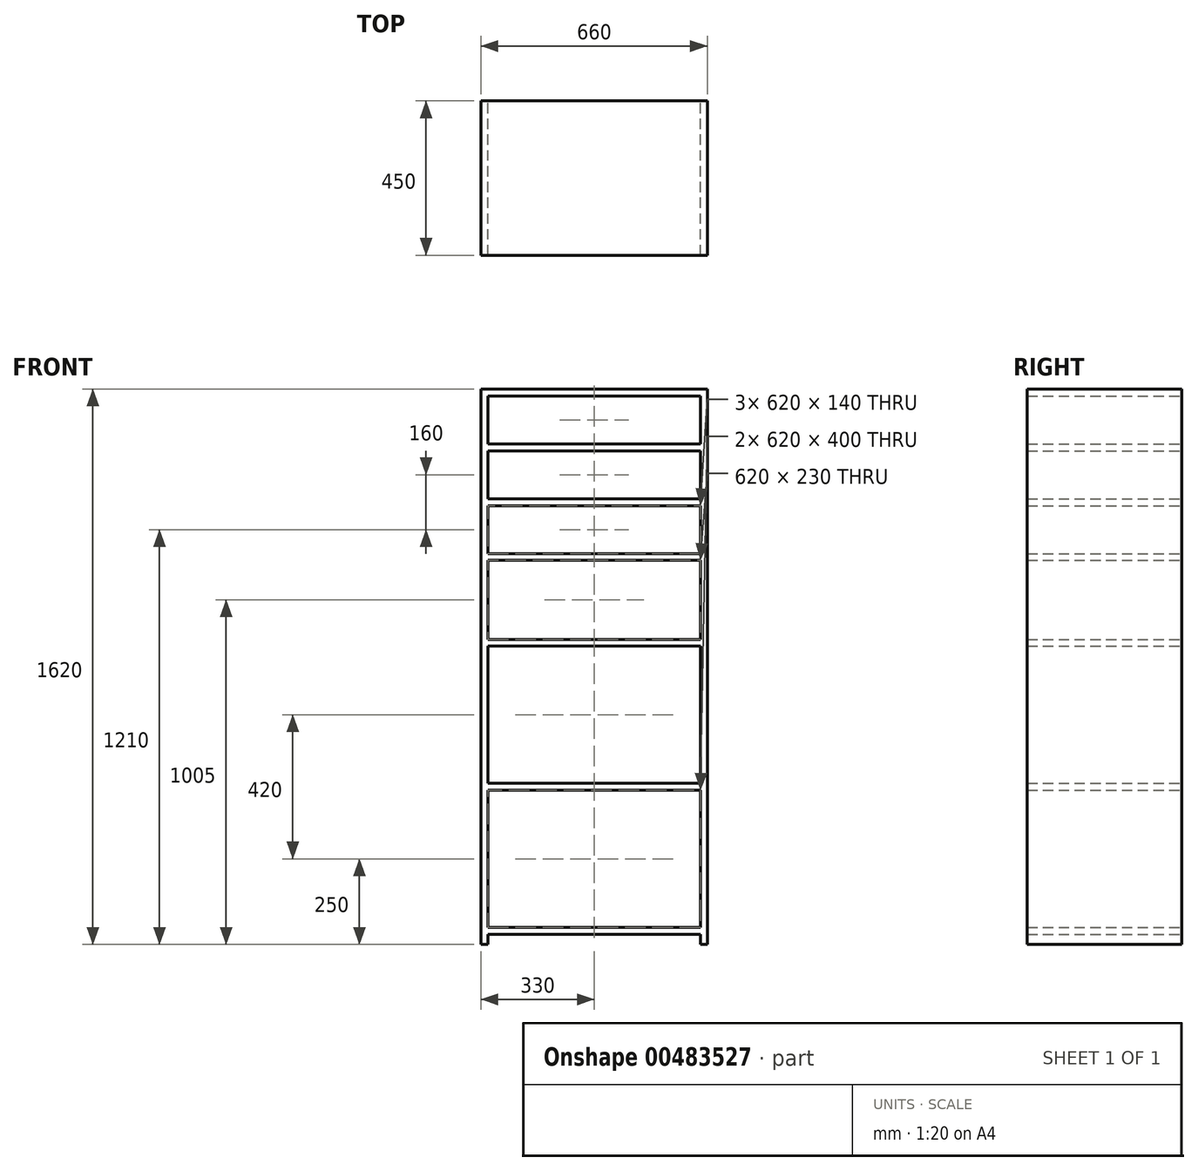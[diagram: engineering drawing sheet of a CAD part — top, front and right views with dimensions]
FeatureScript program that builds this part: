
annotation { "Feature Type Name" : "Feature", "Feature Type Description" : "" }
export const myFeature = defineFeature(function(context is Context, id is Id, definition is map)
    precondition{}
    {
        {
            var Q0;
            Q0=qCreatedBy(makeId("Front.planeOp"),FACE);
            var sketch = newSketch(context, id + "F0", { "sketchPlane" : qUnion([Q0])});
            skLineSegment(sketch, "E0", {"start": v(0, 0) * mm, "end": v(0, 1620) * mm});
            skLineSegment(sketch, "E1", {"start": v(0, 1620) * mm, "end": v(660, 1620) * mm});
            skLineSegment(sketch, "E2", {"start": v(660, 1620) * mm, "end": v(660, 0) * mm});
            skLineSegment(sketch, "E3", {"start": v(660, 0) * mm, "end": v(640, 0) * mm});
            skLineSegment(sketch, "E4", {"start": v(640, 0) * mm, "end": v(640, 30) * mm});
            skLineSegment(sketch, "E5", {"start": v(640, 1600) * mm, "end": v(20, 1600) * mm});
            skLineSegment(sketch, "E6", {"start": v(20, 1600) * mm, "end": v(20, 1460) * mm});
            skLineSegment(sketch, "E7", {"start": v(20, 0) * mm, "end": v(0, 0) * mm});
            skLineSegment(sketch, "E8", {"start": v(640, 1460) * mm, "end": v(20, 1460) * mm});
            skLineSegment(sketch, "E9", {"start": v(640, 1440) * mm, "end": v(20, 1440) * mm});
            skLineSegment(sketch, "E10", {"start": v(640, 1300) * mm, "end": v(20, 1300) * mm});
            skLineSegment(sketch, "E11", {"start": v(640, 1280) * mm, "end": v(20, 1280) * mm});
            skLineSegment(sketch, "E12", {"start": v(640, 1140) * mm, "end": v(20, 1140) * mm});
            skLineSegment(sketch, "E13", {"start": v(640, 1120) * mm, "end": v(20, 1120) * mm});
            skLineSegment(sketch, "E14.trimOffspring", {"start": v(640, 1460) * mm, "end": v(640, 1600) * mm});
            skLineSegment(sketch, "E15.trimOffspring", {"start": v(20, 1440) * mm, "end": v(20, 1300) * mm});
            skLineSegment(sketch, "E16.trimOffspring", {"start": v(20, 1280) * mm, "end": v(20, 1140) * mm});
            skLineSegment(sketch, "E17.trimOffspring", {"start": v(640, 1300) * mm, "end": v(640, 1440) * mm});
            skLineSegment(sketch, "E18.trimOffspring", {"start": v(640, 1140) * mm, "end": v(640, 1280) * mm});
            skLineSegment(sketch, "E19.trimOffspring", {"start": v(20, 1120) * mm, "end": v(20, 890) * mm});
            skLineSegment(sketch, "E20", {"start": v(20, 30) * mm, "end": v(640, 30) * mm});
            skLineSegment(sketch, "E21", {"start": v(20, 50) * mm, "end": v(640, 50) * mm});
            skLineSegment(sketch, "E22", {"start": v(20, 450) * mm, "end": v(640, 450) * mm});
            skLineSegment(sketch, "E23", {"start": v(640, 470) * mm, "end": v(20, 470) * mm});
            skLineSegment(sketch, "E24.trimOffspring", {"start": v(20, 450) * mm, "end": v(20, 50) * mm});
            skLineSegment(sketch, "E25.trimOffspring", {"start": v(20, 30) * mm, "end": v(20, 0) * mm});
            skLineSegment(sketch, "E26.trimOffspring", {"start": v(640, 50) * mm, "end": v(640, 450) * mm});
            skLineSegment(sketch, "E27.trimOffspring", {"start": v(640, 470) * mm, "end": v(640, 870) * mm});
            skLineSegment(sketch, "E28", {"start": v(20, 870) * mm, "end": v(640, 870) * mm});
            skLineSegment(sketch, "E29", {"start": v(20, 890) * mm, "end": v(640, 890) * mm});
            skLineSegment(sketch, "E30.trimOffspring", {"start": v(20, 870) * mm, "end": v(20, 470) * mm});
            skLineSegment(sketch, "E31.trimOffspring", {"start": v(640, 890) * mm, "end": v(640, 1120) * mm});
            skSolve(sketch);
        }
        {
            var Q0;
            Q0 = qSketchRegion(id + "F0", true);
            extrude(context, id + "F1", {"entities" : qUnion([Q0]), "depth" : 450 * mm});
        }
    });
